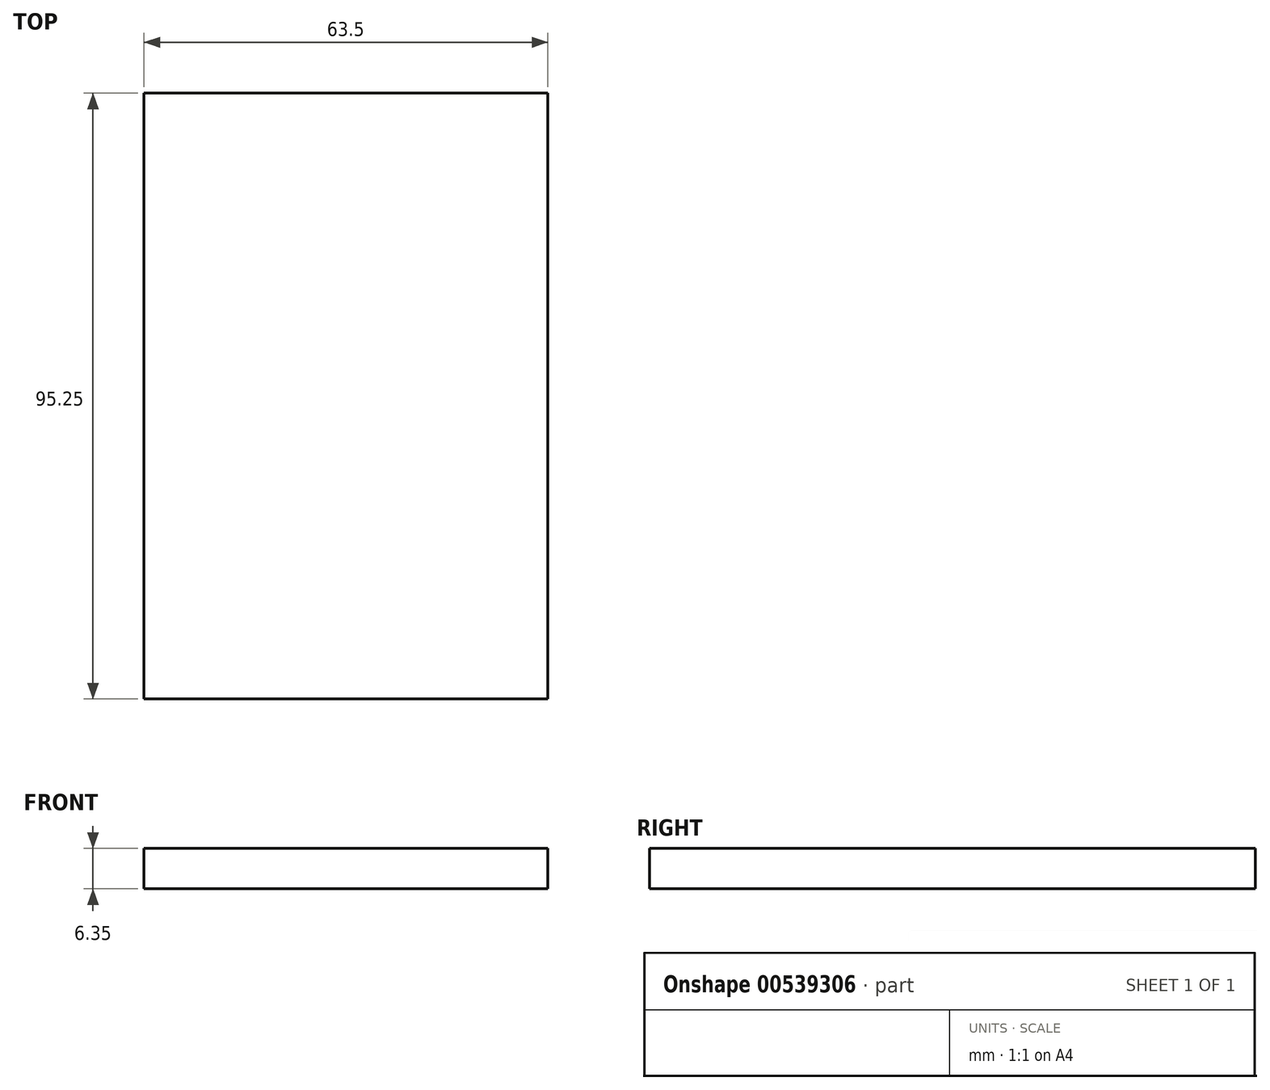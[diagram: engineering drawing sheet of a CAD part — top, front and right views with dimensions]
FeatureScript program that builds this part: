
annotation { "Feature Type Name" : "Feature", "Feature Type Description" : "" }
export const myFeature = defineFeature(function(context is Context, id is Id, definition is map)
    precondition{}
    {
        {
            var Q0;
            Q0=qCreatedBy(makeId("Top.planeOp"),FACE);
            var sketch = newSketch(context, id + "F0", { "sketchPlane" : qUnion([Q0])});
            skLineSegment(sketch, "E0.bottom", {"start": v(-47.96, -11.07) * mm, "end": v(15.54, -11.07) * mm});
            skLineSegment(sketch, "E0.top", {"start": v(-47.96, 84.18) * mm, "end": v(15.54, 84.18) * mm});
            skLineSegment(sketch, "E0.left", {"start": v(-47.96, -11.07) * mm, "end": v(-47.96, 84.18) * mm});
            skLineSegment(sketch, "E0.right", {"start": v(15.54, -11.07) * mm, "end": v(15.54, 84.18) * mm});
            skSolve(sketch);
        }
        {
            var Q0;
            Q0 = qSketchRegion(id + "F0", true);
            extrude(context, id + "F1", {"entities" : qUnion([Q0]), "depth" : 6.35 * mm, "offsetDistance" : 25.4 * mm});
        }
    });
